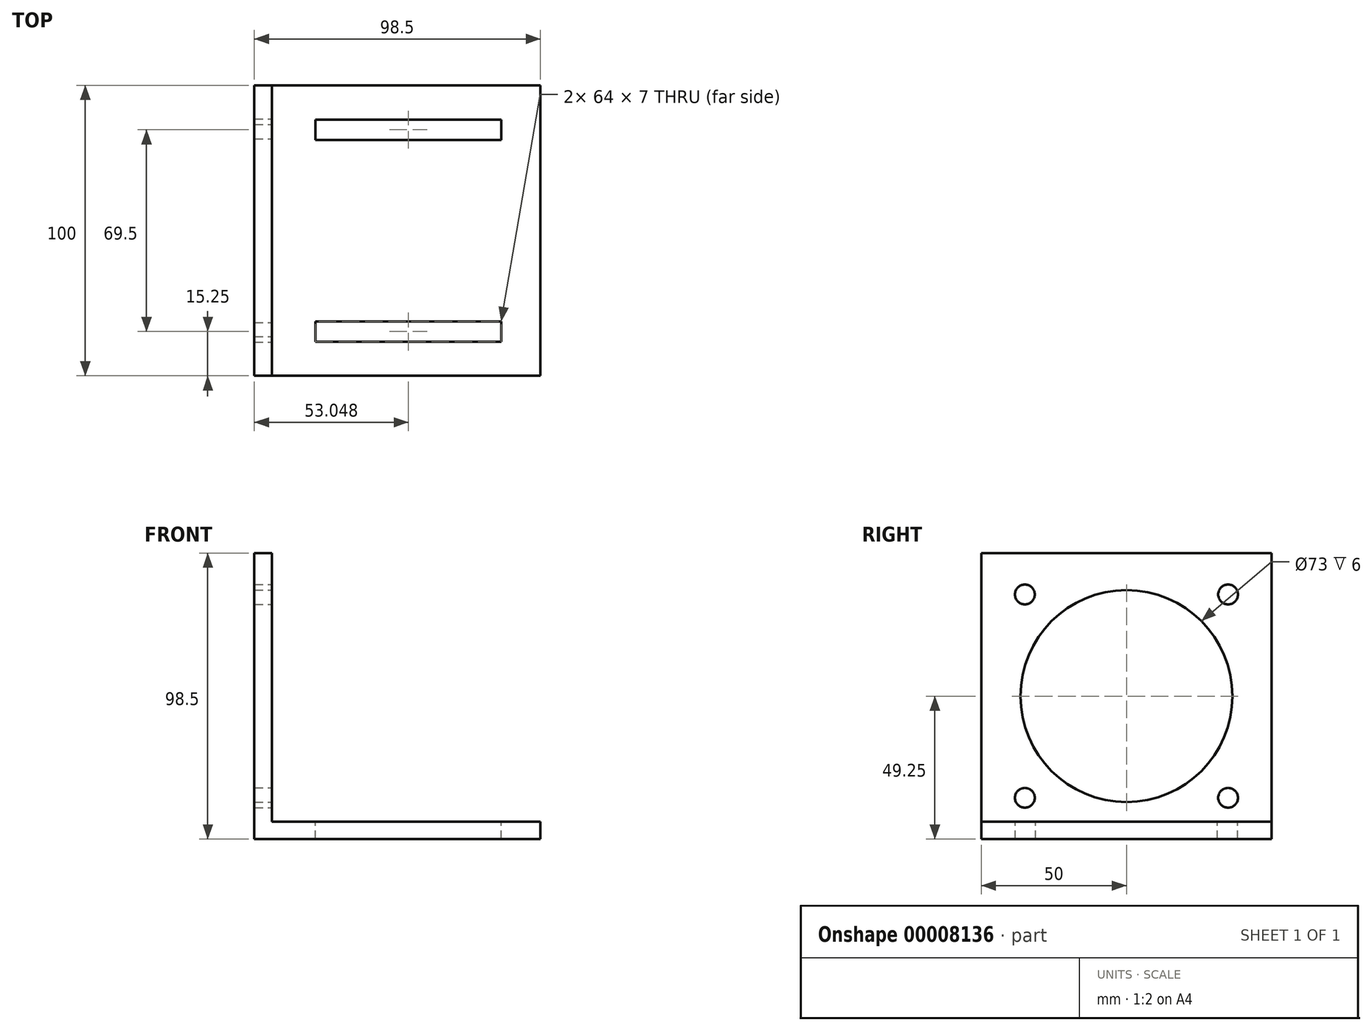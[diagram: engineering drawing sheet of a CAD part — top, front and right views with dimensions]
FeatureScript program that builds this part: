
annotation { "Feature Type Name" : "Feature", "Feature Type Description" : "" }
export const myFeature = defineFeature(function(context is Context, id is Id, definition is map)
    precondition{}
    {
        {
            var Q0;
            Q0=qCreatedBy(makeId("Top.planeOp"),FACE);
            var sketch = newSketch(context, id + "F0", { "sketchPlane" : qUnion([Q0])});
            skLineSegment(sketch, "E0.bottom", {"start": v(-50.76, 32.24) * mm, "end": v(-44.76, 32.24) * mm});
            skLineSegment(sketch, "E0.top", {"start": v(-50.76, -67.76) * mm, "end": v(47.74, -67.76) * mm});
            skLineSegment(sketch, "E0.left", {"start": v(-50.76, 32.24) * mm, "end": v(-50.76, -67.76) * mm});
            skLineSegment(sketch, "E0.right", {"start": v(47.74, 32.24) * mm, "end": v(47.74, -67.76) * mm});
            skLineSegment(sketch, "E1", {"start": v(-44.76, 32.24) * mm, "end": v(47.74, 32.24) * mm});
            skLineSegment(sketch, "E2", {"start": v(-44.76, 32.24) * mm, "end": v(-44.76, -67.76) * mm});
            skSolve(sketch);
        }
        {
            var Q0;
            Q0=makeQuery(id+"F0.imprint","IMPRINT",FACE,{"disambiguationData":[TD([[makeQuery(id+"F0.imprint","IMPRINT",EDGE,{"derivedFrom":sQuery(id+"F0.wireOp",EDGE,"E0.bottom")}),-1.0]])]});
            extrude(context, id + "F1", {"entities" : qUnion([Q0]), "depth" : 98.5 * mm});
        }
        {
            var Q0;
            {var subQ1=sQuery(id+"F0.wireOp",EDGE,"E0.right");Q0=makeQuery(id+"F0.imprint","IMPRINT",FACE,{"disambiguationData":[TD([[makeQuery(id+"F0.imprint","IMPRINT",EDGE,{"derivedFrom":subQ1}),-1.0]])]});}
            extrude(context, id + "F2", {"entities" : qUnion([Q0]), "operationType" : NewBodyOperationType.ADD, "depth" : 6 * mm});
        }
        {
            var Q0;
            Q0=makeQuery(id+"F1.opExtrude","SWEPT_FACE",FACE,{"disambiguationData":[OSD([sQuery(id+"F0.wireOp",EDGE,"E2")])]});
            var sketch = newSketch(context, id + "F3", { "sketchPlane" : qUnion([Q0])});
            skCircle(sketch, "E3", {"center": v(-17.76, 49.25) * mm, "radius": 36.5 * mm});
            skPoint(sketch, "E4", {"position": v(-17.76, 98.5) * mm});
            skPoint(sketch, "E5", {"position": v(-67.76, 52.25) * mm});
            skCircle(sketch, "E6", {"center": v(-52.76, 14.25) * mm, "radius": 3.4 * mm});
            skCircle(sketch, "E7.0.1.0", {"center": v(-52.76, 84.25) * mm, "radius": 3.4 * mm});
            skCircle(sketch, "E7.1.0.0", {"center": v(17.24, 14.25) * mm, "radius": 3.4 * mm});
            skCircle(sketch, "E7.1.1.0", {"center": v(17.24, 84.25) * mm, "radius": 3.4 * mm});
            skLineSegment(sketch, "E7.direction1", {"start": v(-52.76, 14.25) * mm, "end": v(17.24, 14.25) * mm, "construction": true});
            skLineSegment(sketch, "E7.direction2", {"start": v(-52.76, 14.25) * mm, "end": v(-52.76, 84.25) * mm, "construction": true});
            skLineSegment(sketch, "E8", {"start": v(17.24, 84.25) * mm, "end": v(17.24, 14.25) * mm, "construction": true});
            skLineSegment(sketch, "E9", {"start": v(17.24, 84.25) * mm, "end": v(-52.76, 84.25) * mm, "construction": true});
            skLineSegment(sketch, "E10", {"start": v(17.24, 49.25) * mm, "end": v(32.24, 49.25) * mm, "construction": true});
            skLineSegment(sketch, "E11", {"start": v(-52.76, 49.25) * mm, "end": v(-67.76, 49.25) * mm, "construction": true});
            skSolve(sketch);
        }
        {
            var Q0;
            Q0=makeQuery(id+"F3.imprint","IMPRINT",FACE,{"disambiguationData":[TD([[makeQuery(id+"F3.imprint","IMPRINT",EDGE,{"derivedFrom":sQuery(id+"F3.wireOp",EDGE,"E7.0.1.0")}),1.0]])]});
            extrude(context, id + "F4", {"entities" : qUnion([Q0]), "operationType" : NewBodyOperationType.REMOVE, "endBound" : BoundingType.THROUGH_ALL, "oppositeDirection" : true, "depth" : 25.4 * mm});
        }
        {
            var Q0;
            Q0=makeQuery(id+"F3.imprint","IMPRINT",FACE,{"disambiguationData":[TD([[makeQuery(id+"F3.imprint","IMPRINT",EDGE,{"derivedFrom":sQuery(id+"F3.wireOp",EDGE,"E7.1.1.0")}),1.0]])]});
            var Q1;
            Q1=sQuery(id+"F3.wireOp",EDGE,"E7.1.1.0");
            extrude(context, id + "F5", {"entities" : qUnion([Q0]), "operationType" : NewBodyOperationType.REMOVE, "surfaceEntities" : qUnion([Q1]), "endBound" : BoundingType.THROUGH_ALL, "oppositeDirection" : true, "depth" : 25.4 * mm});
        }
        {
            var Q0;
            Q0=makeQuery(id+"F3.imprint","IMPRINT",FACE,{"disambiguationData":[TD([[makeQuery(id+"F3.imprint","IMPRINT",EDGE,{"derivedFrom":sQuery(id+"F3.wireOp",EDGE,"E6")}),1.0]])]});
            var Q1;
            Q1=sQuery(id+"F3.wireOp",EDGE,"E6");
            extrude(context, id + "F6", {"entities" : qUnion([Q0]), "operationType" : NewBodyOperationType.REMOVE, "surfaceEntities" : qUnion([Q1]), "endBound" : BoundingType.THROUGH_ALL, "oppositeDirection" : true, "depth" : 25.4 * mm});
        }
        {
            var Q0;
            Q0=makeQuery(id+"F3.imprint","IMPRINT",FACE,{"disambiguationData":[TD([[makeQuery(id+"F3.imprint","IMPRINT",EDGE,{"derivedFrom":sQuery(id+"F3.wireOp",EDGE,"E7.1.0.0")}),1.0]])]});
            extrude(context, id + "F7", {"entities" : qUnion([Q0]), "operationType" : NewBodyOperationType.REMOVE, "endBound" : BoundingType.THROUGH_ALL, "oppositeDirection" : true, "depth" : 25.4 * mm});
        }
        {
            var Q0;
            Q0=makeQuery(id+"F3.imprint","IMPRINT",FACE,{"disambiguationData":[TD([[makeQuery(id+"F3.imprint","IMPRINT",EDGE,{"derivedFrom":sQuery(id+"F3.wireOp",EDGE,"E3")}),1.0]])]});
            var Q1;
            Q1=sQuery(id+"F3.wireOp",EDGE,"E3");
            extrude(context, id + "F8", {"entities" : qUnion([Q0]), "operationType" : NewBodyOperationType.REMOVE, "surfaceEntities" : qUnion([Q1]), "endBound" : BoundingType.THROUGH_ALL, "oppositeDirection" : true, "depth" : 25.4 * mm});
        }
        {
            var Q0;
            Q0=makeQuery(id+"F2.opExtrude","CAP_FACE",FACE,{"disambiguationData":[OSD([sQuery(id+"F0.wireOp",EDGE,"E0.top"),sQuery(id+"F0.wireOp",EDGE,"E0.right"),sQuery(id+"F0.wireOp",EDGE,"E1"),sQuery(id+"F0.wireOp",EDGE,"E2")])],"isStart":false});
            var sketch = newSketch(context, id + "F9", { "sketchPlane" : qUnion([Q0])});
            skLineSegment(sketch, "E12.bottom", {"start": v(-29.71, 20.49) * mm, "end": v(34.29, 20.49) * mm});
            skLineSegment(sketch, "E12.top", {"start": v(-29.71, 13.49) * mm, "end": v(34.29, 13.49) * mm});
            skLineSegment(sketch, "E12.left", {"start": v(-29.71, 20.49) * mm, "end": v(-29.71, 13.49) * mm});
            skLineSegment(sketch, "E12.right", {"start": v(34.29, 20.49) * mm, "end": v(34.29, 13.49) * mm});
            skLineSegment(sketch, "E13.0.1.0", {"start": v(-29.71, -49.01) * mm, "end": v(34.29, -49.01) * mm});
            skLineSegment(sketch, "E13.0.1.1", {"start": v(-29.71, -56.01) * mm, "end": v(34.29, -56.01) * mm});
            skLineSegment(sketch, "E13.0.1.2", {"start": v(34.29, -49.01) * mm, "end": v(34.29, -56.01) * mm});
            skLineSegment(sketch, "E13.0.1.3", {"start": v(-29.71, -49.01) * mm, "end": v(-29.71, -56.01) * mm});
            skLineSegment(sketch, "E13.direction1", {"start": v(-29.71, 20.49) * mm, "end": v(-4.31, 20.49) * mm, "construction": true});
            skLineSegment(sketch, "E13.direction2", {"start": v(-29.71, 20.49) * mm, "end": v(-29.71, -49.01) * mm, "construction": true});
            skSolve(sketch);
        }
        {
            var Q0;
            Q0=makeQuery(id+"F9.imprint","IMPRINT",FACE,{"disambiguationData":[TD([[makeQuery(id+"F9.imprint","IMPRINT",EDGE,{"derivedFrom":sQuery(id+"F9.wireOp",EDGE,"E12.bottom")}),-1.0]])]});
            var Q1;
            Q1=makeQuery(id+"F9.imprint","IMPRINT",FACE,{"disambiguationData":[TD([[makeQuery(id+"F9.imprint","IMPRINT",EDGE,{"derivedFrom":sQuery(id+"F9.wireOp",EDGE,"E13.0.1.0")}),-1.0]])]});
            extrude(context, id + "F10", {"entities" : qUnion([Q0, Q1]), "operationType" : NewBodyOperationType.REMOVE, "oppositeDirection" : true, "depth" : 25.4 * mm});
        }
    });
